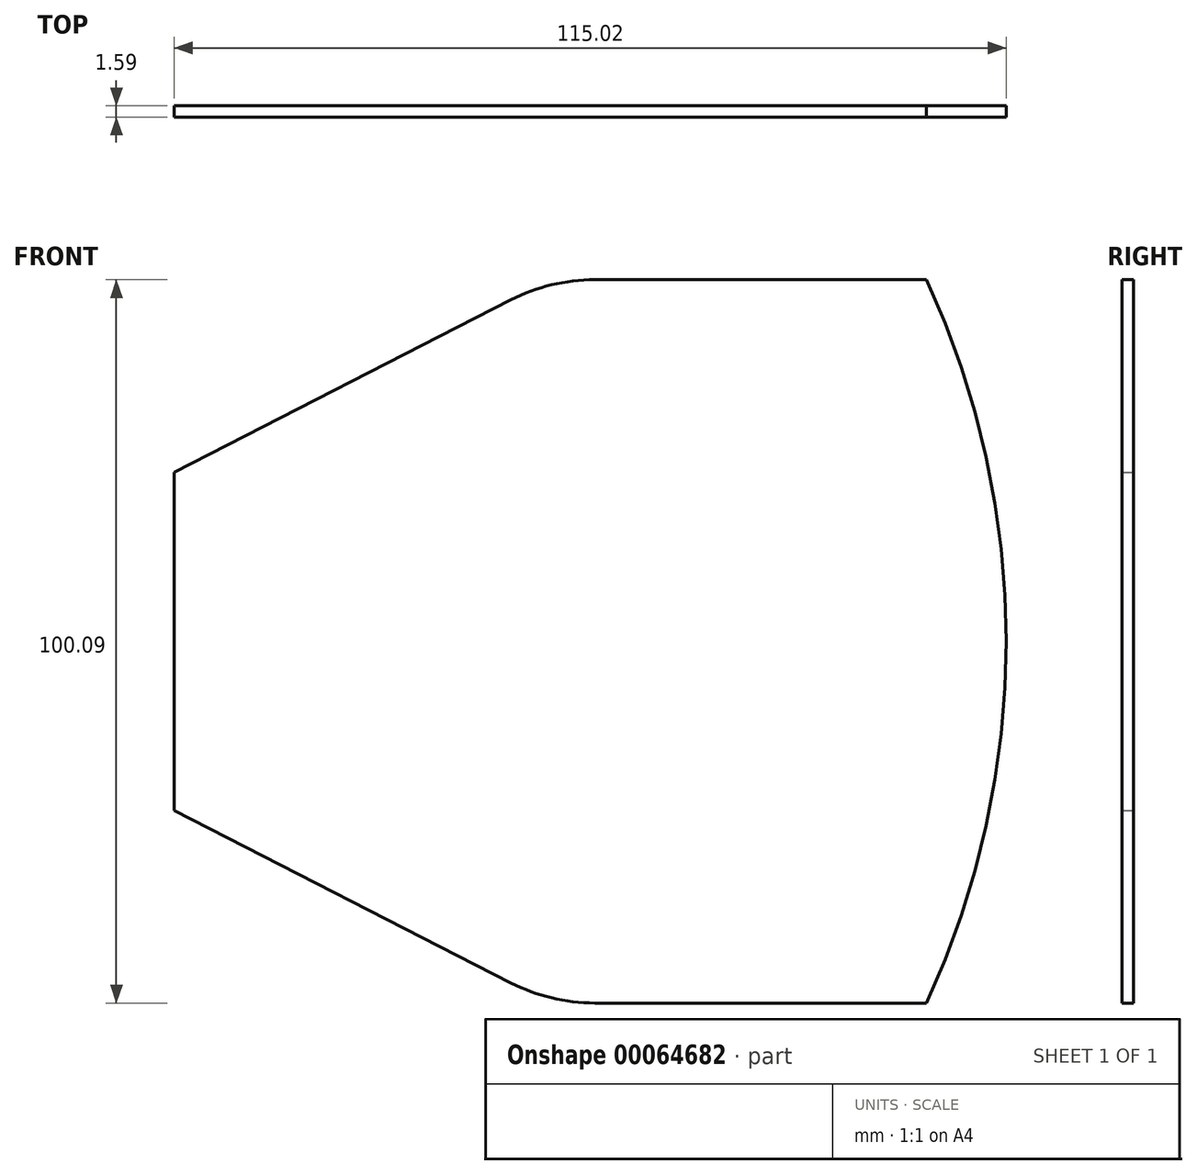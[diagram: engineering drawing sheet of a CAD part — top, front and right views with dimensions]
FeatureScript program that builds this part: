
annotation { "Feature Type Name" : "Feature", "Feature Type Description" : "" }
export const myFeature = defineFeature(function(context is Context, id is Id, definition is map)
    precondition{}
    {
        {
            var Q0;
            Q0=qCreatedBy(makeId("Front.planeOp"),FACE);
            var sketch = newSketch(context, id + "F0", { "sketchPlane" : qUnion([Q0])});
            skLineSegment(sketch, "E0", {"start": v(-2.84, -91.85) * mm, "end": v(-2.84, -45.03) * mm});
            skLineSegment(sketch, "E1", {"start": v(55.29, -18.4) * mm, "end": v(101.15, -18.4) * mm});
            skLineSegment(sketch, "E2", {"start": v(55.29, -118.49) * mm, "end": v(101.15, -118.49) * mm});
            skLineSegment(sketch, "E3", {"start": v(-2.84, -68.44) * mm, "end": v(112.18, -68.44) * mm, "construction": true});
            skArc(sketch, "E4", {"start": v(101.15, -118.49) * mm, "mid": v(112.18, -68.44) * mm, "end": v(101.15, -18.4) * mm});
            skLineSegment(sketch, "E5", {"start": v(43.7, -21.19) * mm, "end": v(-2.84, -45.03) * mm});
            skPoint(sketch, "E6.orphan", {"position": v(-2.84, -18.4) * mm});
            skLineSegment(sketch, "E7", {"start": v(43.7, -115.7) * mm, "end": v(-2.84, -91.85) * mm});
            skPoint(sketch, "E8.orphan", {"position": v(-2.84, -118.49) * mm});
            skPoint(sketch, "E9.visualSharp", {"position": v(49.16, -18.4) * mm});
            skArc(sketch, "E9.filletArc", {"start": v(55.29, -18.4) * mm, "mid": v(49.33, -19.1) * mm, "end": v(43.7, -21.19) * mm});
            skPoint(sketch, "E10.visualSharp", {"position": v(49.16, -118.49) * mm});
            skArc(sketch, "E10.filletArc", {"start": v(43.7, -115.7) * mm, "mid": v(49.33, -117.78) * mm, "end": v(55.29, -118.49) * mm});
            skSolve(sketch);
        }
        {
            var Q0;
            Q0=makeQuery(id+"F0.imprint","IMPRINT",FACE,{"disambiguationData":[TD([[makeQuery(id+"F0.imprint","IMPRINT",EDGE,{"derivedFrom":sQuery(id+"F0.wireOp",EDGE,"E0")}),-1.0]])]});
            extrude(context, id + "F1", {"entities" : qUnion([Q0]), "depth" : 1.59 * mm});
        }
    });
